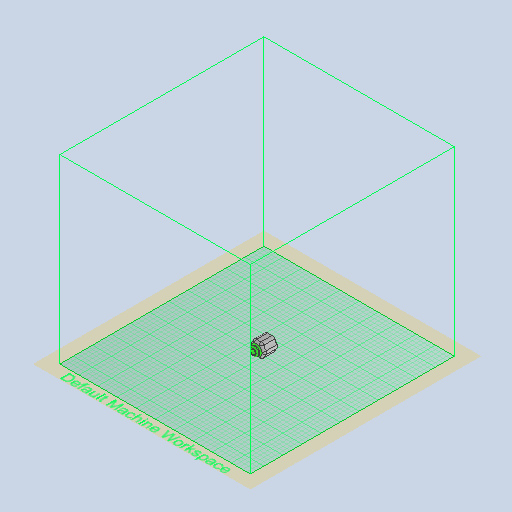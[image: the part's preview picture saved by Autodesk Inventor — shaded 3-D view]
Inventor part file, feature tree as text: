
AUTODESK INVENTOR PART (.ipt)
format: ipt  version: 2022 (Build 260153000, 153)  size: 678,912 bytes
history: native  units: mm
features: extrude x3, fillet x3, sketch x2, chamfer x1
ambient origin geometry x8: Origin, YZ Plane, XZ Plane, XY Plane, X Axis, Y Axis, Z Axis, Center Point
bodies: Solid1 (feature_tree)
feature tree (9):
  extrude  "Extrusion1"  Depth=30.0mm TaperAngle=0.0deg
  extrude  "Extrusion2"  Depth=5.25mm
  extrude  "Extrusion3"  Depth=5.25mm TaperAngle=0.0deg
  fillet  "Fillet1"  Radius=10.2mm
  fillet  "Fillet2"  Radius=20.0mm
  fillet  "Fillet3"  Radius=8.0mm
  chamfer  "Chamfer2"  Distance=3.0mm
  sketch  "Sketch2"  dims[d0=5.2mm d1=30.0mm d2=0.0mm]
  sketch  "Sketch3"  dims[d3=40.0mm d4=8.1mm d5=5.0mm d6=0.0mm d7=10.2mm d8=20.0mm d9=8.0mm d10=0.0mm d11=3.0mm d15=60.0mm d17=360.0deg d19=20.0mm d20=5.25mm d21=5.25mm d22=1.0mm d23=2.0mm d24=45.0deg]
